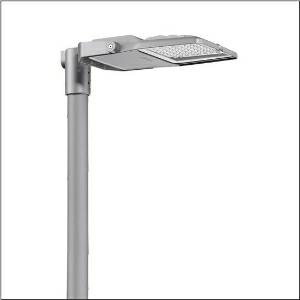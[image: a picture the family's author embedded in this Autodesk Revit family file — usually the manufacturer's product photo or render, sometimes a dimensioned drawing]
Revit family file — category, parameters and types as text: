
# Revit family: floodlight_fl_21_iq_mini___pl33t_5xa7771b4f3a_1cb2
name_source: partatom
category: Lighting Fixtures
units: mm (PartAtom-declared; Revit-internal decimal feet)

## family parameters
Cut with Voids When Loaded = No
Host = Face
Light Source = No
Part Type = Normal
Room Calculation Point = No
Round Connector Dimension = Use Diameter
Shared = No

## types (1)
- --- (1 x LED, 6420 lm, 45.5 W, 4000K)
    Apparent Load = 46 VA
    CIE Flux Codes = 26 75 99 100 100
    Color Rendering = 70
    Color Temperature = 4000K
    Default Elevation = 1800 mm
    Description = Floodlight FL 21 iQ mini, floodlight, primary light control with lens, of PMMA, primary optical cover: protective disc, of toughened safety glass, transparent, light distribution: PL33T, light emission: direct distribution, installation type: surface-mounted, LED, High Power LED, rated luminous flux: 6.420lm, luminous efficacy: 141lm/W, light colour: 740, colour temperature: 4000K, control gear: iQ Comfort/DALI, control: Auto-Match, Temp-Guard, Lumen-Switch, Night-Set, Smart-Wire, Light-Fading, Desk-Remote (wireless, voltage-free reading and setting of iQ features in the workshop via application-optimized NFC function/RFID function), optimised constant luminous flux control (CLO 2.0), with terminal, 6-pole, mains connection: 220..240V, AC, 50/60Hz, start of lifetime: 46W, end of service life: 48W, reduction: 22W, luminaire housing, of diecast aluminium, powder-coated, Siteco® metallic grey (DB 702S), corrosivity category C5 mid according to DIN EN ISO 12944, suitable for swimming pools, chlorine-resistant, sealing non-destructively replaceable, please order mast flange separately, mast bracket, of steel, galvanised, powder-coated, Siteco® metallic grey (DB 702S), protection rating (complete): IP66, insulation class (complete): insulation class II (safety insulation), certification: CE, ENEC, VDE, protection symbol: D, impact resistance: IK08, permissible operating ambient temperature: -40..+40°C, permissible operating ambient temperature for outdoor applications: -40..+50°C, standard: DIN EN 12944, LABS conformity tested according to VDMA 24364:2018-05, packaging unit: 1 piece

Light Distribution: PL33T
    Height = 70 mm
    Lamp = 1 x LED
    Lamp Light Flux = 6420 lm
    Lamp Power = 45.5 W
    Lamp count = 1
    Length = 485 mm
    Luminous efficacy = 141 lm/W
    Manufacturer = Siteco
    ModVariant = No
    Model = 5XA7771B4F3A
    Number of Poles = 1
    OnlyDefault = Yes
    Power Factor = 1
    Product Name = Floodlight FL 21 iQ mini | PL33T
    Product group = floodlight | pylon annexe
    ProductGroupID = 6200
    Protection Class = Protection class II
    Protection Degree = IP 66
    RLX_Detail_Level = 1
    RLX_Emergency_Light_Flux = 0 lm
    RLX_Emergency_Type = 0
    RLX_Emergency_Type_DB = No
    RlxData = <blob elided: 101221 chars, md5=6ebb709c>
    Socket = socket
    Standby Power = 0 W
    System Light Flux = 6420 lm
    System Power = 46 W
    Type Comments = factory setting: luminous flux: 100 % | dim-lin: 254 | 463 mA
    Type Image = l_1007125.jpg
    URL = http://relux.com
    VarID = @adj_150176
    Voltage = 0 V
    Weight = 0.00 kg
    Width = 337 mm

## geometry (parser evidence)
native form markers: Blend x4, Sweep x13
no freeform markers — native parametric forms only
